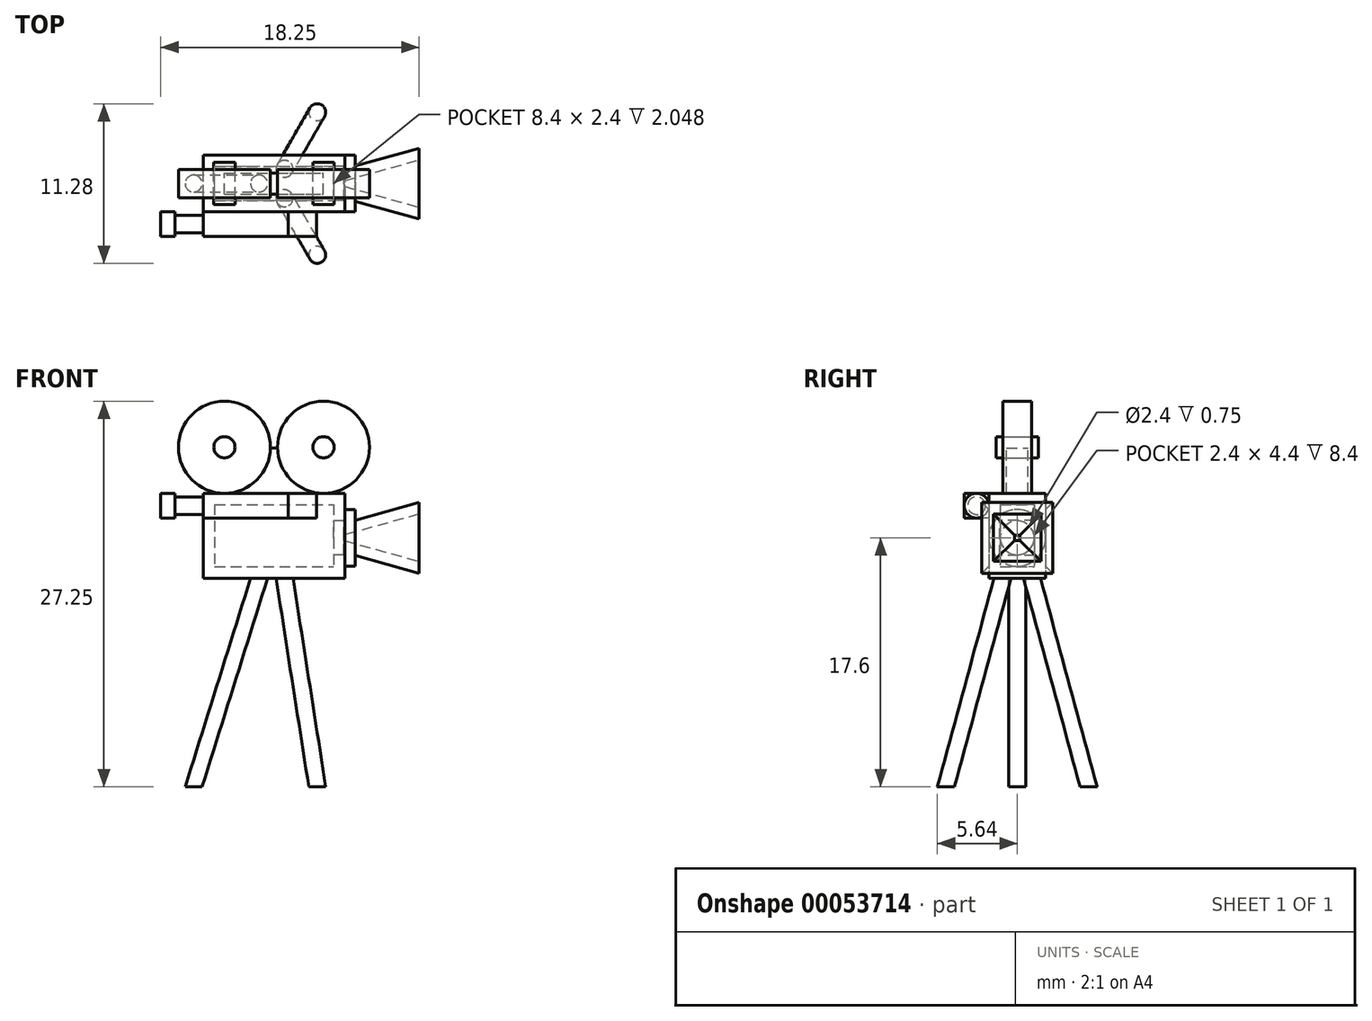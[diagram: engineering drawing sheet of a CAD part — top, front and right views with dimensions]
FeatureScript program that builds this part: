
annotation { "Feature Type Name" : "Feature", "Feature Type Description" : "" }
export const myFeature = defineFeature(function(context is Context, id is Id, definition is map)
    precondition{}
    {
        {
            var Q0;
            Q0=qCreatedBy(makeId("Front.planeOp"),FACE);
            var sketch = newSketch(context, id + "F0", { "sketchPlane" : qUnion([Q0])});
            skLineSegment(sketch, "E0.bottom", {"start": v(-5.15, 3.15) * mm, "end": v(4.85, 3.15) * mm});
            skLineSegment(sketch, "E0.top", {"start": v(-5.15, -2.85) * mm, "end": v(4.85, -2.85) * mm});
            skLineSegment(sketch, "E0.left", {"start": v(-5.15, 3.15) * mm, "end": v(-5.15, -2.85) * mm});
            skLineSegment(sketch, "E0.right", {"start": v(4.85, 3.15) * mm, "end": v(4.85, -2.85) * mm});
            skSolve(sketch);
        }
        {
            var Q0;
            Q0 = qSketchRegion(id + "F0", true);
            extrude(context, id + "F1", {"entities" : qUnion([Q0]), "endBound" : BoundingType.SYMMETRIC, "depth" : 4 * mm});
        }
        {
            var Q0;
            Q0=qCreatedBy(makeId("Front.planeOp"),FACE);
            var sketch = newSketch(context, id + "F2", { "sketchPlane" : qUnion([Q0])});
            skCircle(sketch, "E1", {"center": v(-3.65, 6.4) * mm, "radius": 3.25 * mm});
            skCircle(sketch, "E2", {"center": v(3.35, 6.4) * mm, "radius": 3.25 * mm});
            skSolve(sketch);
        }
        {
            var Q0;
            Q0 = qSketchRegion(id + "F2", true);
            extrude(context, id + "F3", {"entities" : qUnion([Q0]), "operationType" : NewBodyOperationType.ADD, "endBound" : BoundingType.SYMMETRIC, "depth" : 2 * mm});
        }
        {
            var Q0;
            Q0=qCreatedBy(makeId("Front.planeOp"),FACE);
            var sketch = newSketch(context, id + "F4", { "sketchPlane" : qUnion([Q0])});
            skArc(sketch, "E3.0", {"start": v(-3.65, 3.15) * mm, "mid": v(-1.37, 4.08) * mm, "end": v(-0.4, 6.34) * mm});
            skArc(sketch, "E4.0", {"start": v(0.1, 6.34) * mm, "mid": v(1.08, 4.08) * mm, "end": v(3.35, 3.15) * mm});
            skLineSegment(sketch, "E5.0", {"start": v(-5.15, 3.15) * mm, "end": v(4.85, 3.15) * mm});
            skLineSegment(sketch, "E6", {"start": v(-0.4, 6.34) * mm, "end": v(0.1, 6.34) * mm});
            skSolve(sketch);
        }
        {
            var Q0;
            Q0 = qSketchRegion(id + "F4", true);
            extrude(context, id + "F5", {"entities" : qUnion([Q0]), "endBound" : BoundingType.SYMMETRIC, "depth" : 1.5 * mm});
        }
        {
            var Q0;
            Q0=qCreatedBy(makeId("Front.planeOp"),FACE);
            var sketch = newSketch(context, id + "F6", { "sketchPlane" : qUnion([Q0])});
            skCircle(sketch, "E7", {"center": v(-3.65, 6.4) * mm, "radius": 0.75 * mm});
            skCircle(sketch, "E8", {"center": v(3.35, 6.4) * mm, "radius": 0.75 * mm});
            skSolve(sketch);
        }
        {
            var Q0;
            Q0 = qSketchRegion(id + "F6", true);
            extrude(context, id + "F7", {"entities" : qUnion([Q0]), "endBound" : BoundingType.SYMMETRIC, "depth" : 3 * mm});
        }
        {
            var Q0;
            Q0=makeQuery(id+"F1.opExtrude","SWEPT_FACE",FACE,{"disambiguationData":[OSD([sQuery(id+"F0.wireOp",EDGE,"E0.right")])]});
            var sketch = newSketch(context, id + "F8", { "sketchPlane" : qUnion([Q0])});
            skCircle(sketch, "E9", {"center": v(0, 0) * mm, "radius": 2 * mm});
            skSolve(sketch);
        }
        {
            var Q0;
            Q0 = qSketchRegion(id + "F8", true);
            extrude(context, id + "F9", {"entities" : qUnion([Q0]), "operationType" : NewBodyOperationType.ADD, "depth" : .75 * mm});
        }
        {
            var Q0;
            Q0=makeQuery(id+"F9.opExtrude","CAP_FACE",FACE,{"disambiguationData":[OSD([sQuery(id+"F8.wireOp",EDGE,"E9")])],"isStart":false});
            var sketch = newSketch(context, id + "F10", { "sketchPlane" : qUnion([Q0])});
            skPoint(sketch, "E10.rect.middle", {"position": v(0, 0) * mm});
            skLineSegment(sketch, "E11.rect.bottom", {"start": v(1.25, -1.25) * mm, "end": v(-1.25, -1.25) * mm});
            skLineSegment(sketch, "E11.rect.top", {"start": v(1.25, 1.25) * mm, "end": v(-1.25, 1.25) * mm});
            skLineSegment(sketch, "E11.rect.left", {"start": v(1.25, -1.25) * mm, "end": v(1.25, 1.25) * mm});
            skLineSegment(sketch, "E11.rect.right", {"start": v(-1.25, -1.25) * mm, "end": v(-1.25, 1.25) * mm});
            skSolve(sketch);
        }
        {
            var Q0;
            Q0=makeQuery(id+"F9.opExtrude","CAP_FACE",FACE,{"disambiguationData":[OSD([sQuery(id+"F8.wireOp",EDGE,"E9")])],"isStart":false});
            cPlane(context, id + "F11", {"entities" : qUnion([Q0]), "cplaneType" : CPlaneType.OFFSET, "offset" : 4.5 * mm, "width" : 150 * mm, "height" : 150 * mm});
        }
        {
            var Q0;
            Q0=qCreatedBy(id+"F11.planeOp",FACE);
            var sketch = newSketch(context, id + "F12", { "sketchPlane" : qUnion([Q0])});
            skLineSegment(sketch, "E12.rect.bottom", {"start": v(2.5, -2.5) * mm, "end": v(-2.5, -2.5) * mm});
            skLineSegment(sketch, "E12.rect.top", {"start": v(2.5, 2.5) * mm, "end": v(-2.5, 2.5) * mm});
            skLineSegment(sketch, "E12.rect.left", {"start": v(2.5, -2.5) * mm, "end": v(2.5, 2.5) * mm});
            skLineSegment(sketch, "E12.rect.right", {"start": v(-2.5, -2.5) * mm, "end": v(-2.5, 2.5) * mm});
            skPoint(sketch, "E12.rect.middle", {"position": v(0, 0) * mm});
            skSolve(sketch);
        }
        {
            var Q1;
            Q1 = qSketchRegion(id + "F12", true);
            var Q2;
            Q2 = qSketchRegion(id + "F10", true);
            loft(context, id + "F13", {"operationType" : NewBodyOperationType.ADD, "sheetProfilesArray" : [{ "sheetProfileEntities" : qUnion([Q1]) }, { "sheetProfileEntities" : qUnion([Q2]) }]});
        }
        {
            var Q0;
            Q0=makeQuery(id+"F13.opLoft","CAP_FACE",FACE,{"disambiguationData":[OSD([makeQuery(id+"F12.imprint","IMPRINT",FACE,{"disambiguationData":[TD([[makeQuery(id+"F12.imprint","IMPRINT",EDGE,{"derivedFrom":sQuery(id+"F12.wireOp",EDGE,"E12.rect.bottom")}),-1.0]])]})])],"isStart":true});
            shell(context, id + "F14", {"entities" : qUnion([Q0]), "thickness" : .8 * mm});
        }
        {
            var Q0;
            Q0=makeQuery(id+"F1.opExtrude","SWEPT_FACE",FACE,{"disambiguationData":[OSD([sQuery(id+"F0.wireOp",EDGE,"E0.left")])]});
            var sketch = newSketch(context, id + "F15", { "sketchPlane" : qUnion([Q0])});
            skLineSegment(sketch, "E13.bottom", {"start": v(2, 3.15) * mm, "end": v(3.75, 3.15) * mm});
            skLineSegment(sketch, "E13.top", {"start": v(2, 1.4) * mm, "end": v(3.75, 1.4) * mm});
            skLineSegment(sketch, "E13.left", {"start": v(2, 3.15) * mm, "end": v(2, 1.4) * mm});
            skLineSegment(sketch, "E13.right", {"start": v(3.75, 3.15) * mm, "end": v(3.75, 1.4) * mm});
            skSolve(sketch);
        }
        {
            var Q0;
            Q0 = qSketchRegion(id + "F15", true);
            extrude(context, id + "F16", {"entities" : qUnion([Q0]), "oppositeDirection" : true, "depth" : 6 * mm});
        }
        {
            var Q0;
            Q0=makeQuery(id+"F16.opExtrude","CAP_FACE",FACE,{"disambiguationData":[OSD([sQuery(id+"F15.wireOp",EDGE,"E13.bottom"),sQuery(id+"F15.wireOp",EDGE,"E13.top"),sQuery(id+"F15.wireOp",EDGE,"E13.left"),sQuery(id+"F15.wireOp",EDGE,"E13.right")])],"isStart":false});
            var sketch = newSketch(context, id + "F17", { "sketchPlane" : qUnion([Q0])});
            skCircle(sketch, "E14", {"center": v(-2.88, 2.28) * mm, "radius": 0.88 * mm});
            skPoint(sketch, "E14.centerSnap0", {"position": v(-2.88, 3.15) * mm});
            skPoint(sketch, "E14.centerSnap1", {"position": v(-2, 2.28) * mm});
            skSolve(sketch);
        }
        {
            var Q0;
            Q0 = qSketchRegion(id + "F17", true);
            extrude(context, id + "F18", {"entities" : qUnion([Q0]), "depth" : 2 * mm});
        }
        {
            var Q0;
            Q0=makeQuery(id+"F16.opExtrude","CAP_FACE",FACE,{"disambiguationData":[OSD([sQuery(id+"F15.wireOp",EDGE,"E13.bottom"),sQuery(id+"F15.wireOp",EDGE,"E13.top"),sQuery(id+"F15.wireOp",EDGE,"E13.left"),sQuery(id+"F15.wireOp",EDGE,"E13.right")])],"isStart":true});
            var sketch = newSketch(context, id + "F19", { "sketchPlane" : qUnion([Q0])});
            skCircle(sketch, "E15", {"center": v(2.88, 2.28) * mm, "radius": 0.62 * mm});
            skPoint(sketch, "E15.centerSnap0", {"position": v(3.75, 2.28) * mm});
            skPoint(sketch, "E15.centerSnap1", {"position": v(2.88, 3.15) * mm});
            skSolve(sketch);
        }
        {
            var Q0;
            Q0 = qSketchRegion(id + "F19", true);
            extrude(context, id + "F20", {"entities" : qUnion([Q0]), "operationType" : NewBodyOperationType.ADD, "depth" : 3 * mm});
        }
        {
            var Q0;
            Q0=makeQuery(id+"F20.opExtrude","CAP_FACE",FACE,{"disambiguationData":[OSD([sQuery(id+"F19.wireOp",EDGE,"E15")])],"isStart":false});
            var sketch = newSketch(context, id + "F21", { "sketchPlane" : qUnion([Q0])});
            skCircle(sketch, "E16", {"center": v(2.88, 2.28) * mm, "radius": 0.88 * mm});
            skSolve(sketch);
        }
        {
            var Q0;
            Q0 = qSketchRegion(id + "F21", true);
            extrude(context, id + "F22", {"entities" : qUnion([Q0]), "operationType" : NewBodyOperationType.ADD, "oppositeDirection" : true, "depth" : 1 * mm});
        }
        {
            var Q0;
            Q0=qCreatedBy(makeId("Right.planeOp"),FACE);
            var sketch = newSketch(context, id + "F23", { "sketchPlane" : qUnion([Q0])});
            skCircle(sketch, "E17", {"center": v(0, 9.34) * mm, "radius": 0.62 * mm});
            skSolve(sketch);
        }
        {
            var Q0;
            Q0=sQuery(id+"F23.wireOp",EDGE,"E17");
            var Q1;
            Q1=makeQuery(id+"F5.opExtrude","SWEPT_EDGE",EDGE,{"disambiguationData":[OSD([sQuery(id+"F4.wireOp",EDGE,"E3.0"),sQuery(id+"F4.wireOp",EDGE,"E6")])]});
            revolve(context, id + "F24", {"bodyType" : ToolBodyType.SURFACE, "surfaceEntities" : qUnion([Q0]), "axis" : qUnion([Q1]), "revolveType" : RevolveType.SYMMETRIC, "angle" : 90 * degree});
        }
        {
            var Q0;
            Q0=makeQuery(id+"F1.opExtrude","SWEPT_FACE",FACE,{"disambiguationData":[OSD([sQuery(id+"F0.wireOp",EDGE,"E0.top")])]});
            var sketch = newSketch(context, id + "F25", { "sketchPlane" : qUnion([Q0])});
            skCircle(sketch, "E18", {"center": v(-1.2, 0) * mm, "radius": 0.6 * mm});
            skSolve(sketch);
        }
        {
            var Q0;
            Q0=qCreatedBy(makeId("Front.planeOp"),FACE);
            var sketch = newSketch(context, id + "F26", { "sketchPlane" : qUnion([Q0])});
            skPoint(sketch, "E19.0", {"position": v(-1.2, -2.85) * mm});
            skLineSegment(sketch, "E20", {"start": v(-1.2, -2.85) * mm, "end": v(-5.82, -17.6) * mm});
            skSolve(sketch);
        }
        {
            var Q0;
            Q0 = qSketchRegion(id + "F25", true);
            var Q1;
            Q1 = qConstructionFilter(qBodyType(qCreatedBy(id + "F26" ,EDGE), BodyType.WIRE), ConstructionObject.NO);
            sweep(context, id + "F27", {"profiles" : qUnion([Q0]), "path" : qUnion([Q1])});
        }
        {
            var Q0;
            Q0=qCreatedBy(makeId("Right.planeOp"),FACE);
            var sketch = newSketch(context, id + "F28", { "sketchPlane" : qUnion([Q0])});
            skLineSegment(sketch, "E21", {"start": v(0, 12.43) * mm, "end": v(0, -11.62) * mm});
            skSolve(sketch);
        }
        {
            var Q0;
            Q0=makeQuery(id+"F27.opSweep","SWEPT_BODY",BODY,{"disambiguationData":[OSD([sQuery(id+"F25.wireOp",EDGE,"E18"),sQuery(id+"F26.wireOp",EDGE,"E20")])]});
            var Q1;
            Q1=sQuery(id+"F28.wireOp",EDGE,"E21");
            circularPattern(context, id + "F29", {"entities" : qUnion([Q0]), "axis" : qUnion([Q1]), "angle" : 120 * degree, "instanceCount" : 3});
        }
    });
